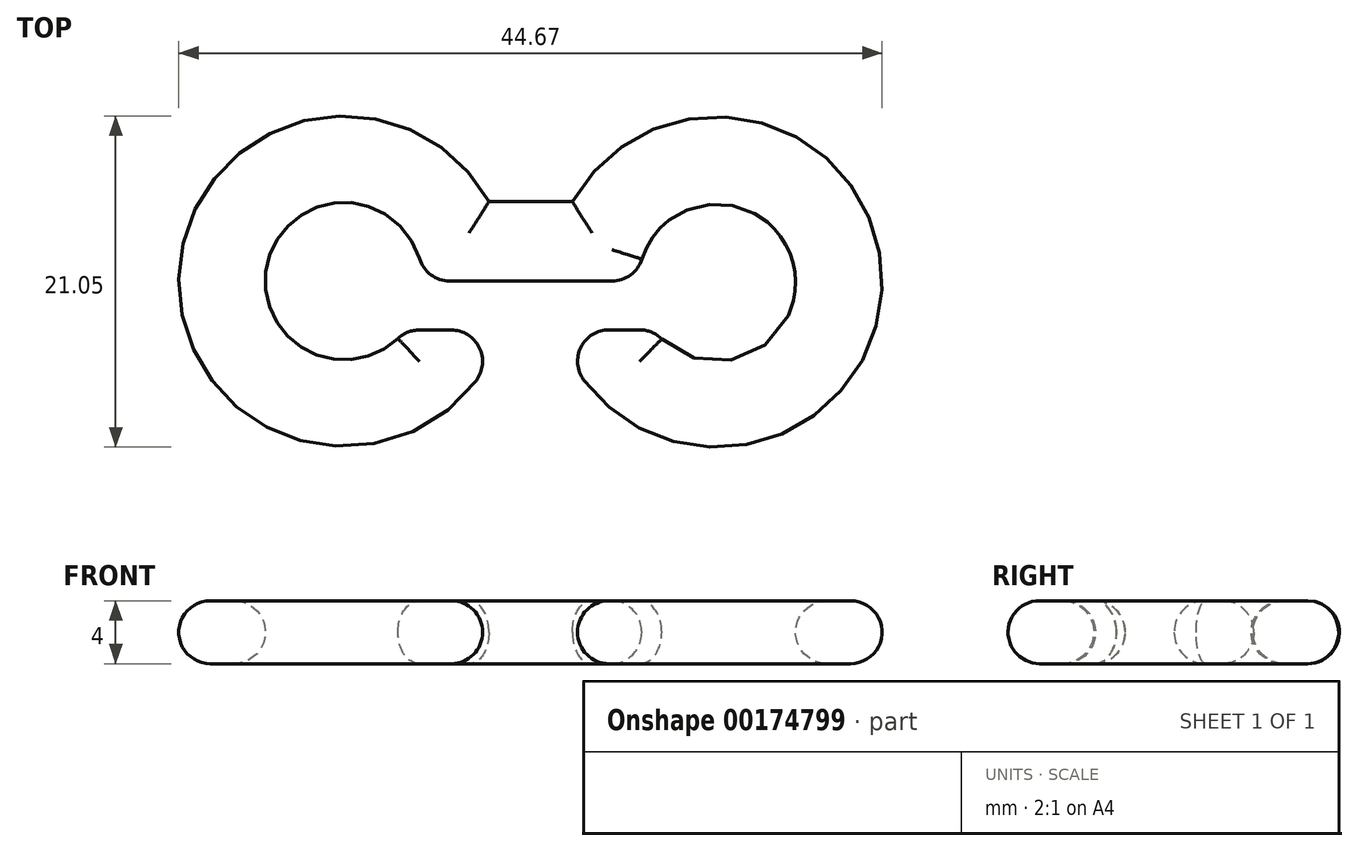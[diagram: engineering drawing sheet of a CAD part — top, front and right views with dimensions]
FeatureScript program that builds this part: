
annotation { "Feature Type Name" : "Feature", "Feature Type Description" : "" }
export const myFeature = defineFeature(function(context is Context, id is Id, definition is map)
    precondition{}
    {
        {
            var Q0;
            Q0=qCreatedBy(makeId("Top.planeOp"),FACE);
            var sketch = newSketch(context, id + "F0", { "sketchPlane" : qUnion([Q0])});
            skArc(sketch, "E0", {"start": v(5, 0) * mm, "mid": v(-4.72, 1.64) * mm, "end": v(3.92, -3.1) * mm});
            skArc(sketch, "E1", {"start": v(10.5, 0) * mm, "mid": v(-9.96, 3.32) * mm, "end": v(8.4, -6.3) * mm});
            skArc(sketch, "E2", {"start": v(15.22, -6.28) * mm, "mid": v(33.65, 3.21) * mm, "end": v(13.17, 0) * mm});
            skArc(sketch, "E3", {"start": v(19.68, -3.1) * mm, "mid": v(28.44, 1.43) * mm, "end": v(18.68, 0) * mm});
            skLineSegment(sketch, "E4", {"start": v(9.2, 5.07) * mm, "end": v(14.5, 5.07) * mm});
            skLineSegment(sketch, "E5", {"start": v(10.5, 0) * mm, "end": v(13.17, 0) * mm});
            skLineSegment(sketch, "E6", {"start": v(10.5, 0) * mm, "end": v(5, 0) * mm});
            skLineSegment(sketch, "E7", {"start": v(13.17, 0) * mm, "end": v(18.68, 0) * mm});
            skLineSegment(sketch, "E8", {"start": v(6.8, -3.1) * mm, "end": v(3.92, -3.1) * mm});
            skLineSegment(sketch, "E9", {"start": v(16.83, -3.1) * mm, "end": v(19.68, -3.1) * mm});
            skPoint(sketch, "E10.start.orphan", {"position": v(11.83, 0) * mm});
            skPoint(sketch, "E11.visualSharp", {"position": v(13.62, -3.1) * mm});
            skArc(sketch, "E11.filletArc", {"start": v(16.83, -3.1) * mm, "mid": v(15.04, -4.2) * mm, "end": v(15.22, -6.28) * mm});
            skPoint(sketch, "E12.visualSharp", {"position": v(10.03, -3.1) * mm});
            skArc(sketch, "E12.filletArc", {"start": v(8.4, -6.3) * mm, "mid": v(8.59, -4.2) * mm, "end": v(6.8, -3.1) * mm});
            skSolve(sketch);
        }
        {
            var Q0;
            Q0 = qSketchRegion(id + "F0", true);
            extrude(context, id + "F1", {"entities" : qUnion([Q0]), "depth" : 4 * mm});
        }
        {
            var Q0;
            Q0=makeQuery(id+"F1.opExtrude","CAP_EDGE",EDGE,{"disambiguationData":[OSD([sQuery(id+"F0.wireOp",EDGE,"E0")])],"isStart":false});
            var Q1;
            Q1=makeQuery(id+"F1.opExtrude","CAP_EDGE",EDGE,{"disambiguationData":[OSD([sQuery(id+"F0.wireOp",EDGE,"E3")])],"isStart":false});
            fillet(context, id + "F2", {"entities" : qUnion([Q0, Q1]), "radius" : 2 * mm, "tangentPropagation" : true, "allowEdgeOverflow" : false});
        }
        {
            var Q0;
            Q0=makeQuery(id+"F1.opExtrude","CAP_EDGE",EDGE,{"disambiguationData":[OSD([sQuery(id+"F0.wireOp",EDGE,"E2")])],"isStart":false});
            var Q1;
            Q1=makeQuery(id+"F1.opExtrude","CAP_EDGE",EDGE,{"disambiguationData":[OSD([sQuery(id+"F0.wireOp",EDGE,"E1")])],"isStart":false});
            fillet(context, id + "F3", {"entities" : qUnion([Q0, Q1]), "radius" : 2 * mm, "tangentPropagation" : true, "allowEdgeOverflow" : false});
        }
        {
            var Q0;
            Q0=makeQuery(id+"F1.opExtrude","CAP_EDGE",EDGE,{"disambiguationData":[OSD([sQuery(id+"F0.wireOp",EDGE,"E5"),sQuery(id+"F0.wireOp",EDGE,"E6"),sQuery(id+"F0.wireOp",EDGE,"E7")])],"isStart":false});
            var Q1;
            Q1=makeQuery(id+"F1.opExtrude","CAP_EDGE",EDGE,{"disambiguationData":[OSD([sQuery(id+"F0.wireOp",EDGE,"E4")])],"isStart":false});
            fillet(context, id + "F4", {"entities" : qUnion([Q0, Q1]), "radius" : 2 * mm, "tangentPropagation" : true, "allowEdgeOverflow" : false});
        }
        {
            var Q0;
            Q0=makeQuery(id+"F1.opExtrude","CAP_EDGE",EDGE,{"disambiguationData":[OSD([sQuery(id+"F0.wireOp",EDGE,"E2")])],"isStart":true});
            fillet(context, id + "F5", {"entities" : qUnion([Q0]), "radius" : 2 * mm, "tangentPropagation" : true, "allowEdgeOverflow" : false});
        }
        {
            var Q0;
            Q0=makeQuery(id+"F1.opExtrude","CAP_EDGE",EDGE,{"disambiguationData":[OSD([sQuery(id+"F0.wireOp",EDGE,"E4")])],"isStart":true});
            fillet(context, id + "F6", {"entities" : qUnion([Q0]), "radius" : 2 * mm, "tangentPropagation" : true, "allowEdgeOverflow" : false});
        }
    });
